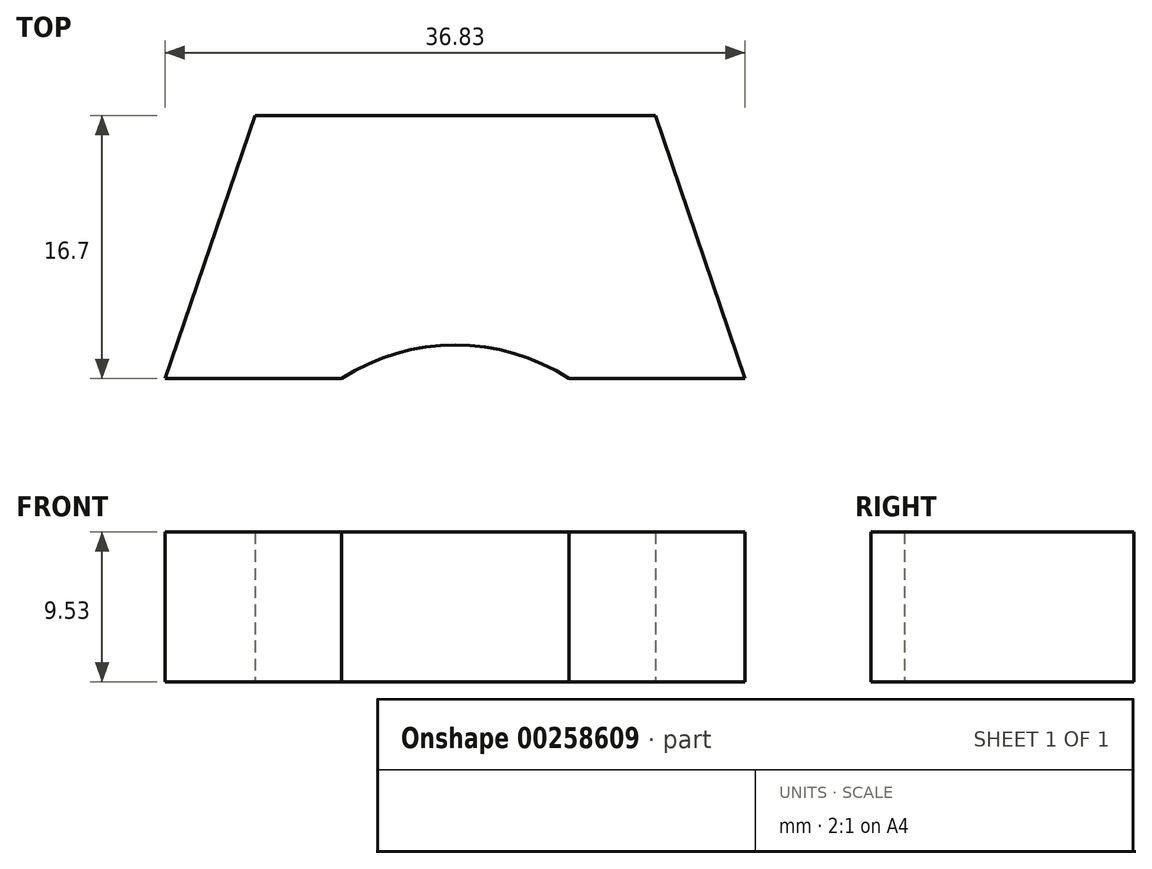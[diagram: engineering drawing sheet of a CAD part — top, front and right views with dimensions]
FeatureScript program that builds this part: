
annotation { "Feature Type Name" : "Feature", "Feature Type Description" : "" }
export const myFeature = defineFeature(function(context is Context, id is Id, definition is map)
    precondition{}
    {
        {
            var Q0;
            Q0=qCreatedBy(makeId("Top.planeOp"),FACE);
            var sketch = newSketch(context, id + "F0", { "sketchPlane" : qUnion([Q0])});
            skLineSegment(sketch, "E0", {"start": v(45.7, 81.96) * mm, "end": v(79.7, 81.96) * mm});
            skLineSegment(sketch, "E1", {"start": v(45.7, 81.96) * mm, "end": v(35.86, 53.26) * mm});
            skLineSegment(sketch, "E2", {"start": v(35.86, 53.26) * mm, "end": v(89.47, 53.26) * mm});
            skLineSegment(sketch, "E3", {"start": v(89.47, 53.26) * mm, "end": v(79.7, 81.96) * mm});
            skLineSegment(sketch, "E4.0", {"start": v(49.98, 75.96) * mm, "end": v(75.4, 75.96) * mm});
            skLineSegment(sketch, "E4.1", {"start": v(49.98, 75.96) * mm, "end": v(44.26, 59.26) * mm});
            skLineSegment(sketch, "E4.2", {"start": v(44.26, 59.26) * mm, "end": v(55.47, 59.26) * mm});
            skLineSegment(sketch, "E4.3", {"start": v(81.09, 59.26) * mm, "end": v(75.4, 75.96) * mm});
            skLineSegment(sketch, "E5", {"start": v(35.86, 53.26) * mm, "end": v(35.86, 42.84) * mm});
            skLineSegment(sketch, "E6", {"start": v(35.86, 42.84) * mm, "end": v(89.47, 42.84) * mm});
            skLineSegment(sketch, "E7", {"start": v(89.47, 42.84) * mm, "end": v(89.47, 53.26) * mm});
            skLineSegment(sketch, "E8", {"start": v(35.86, 48.05) * mm, "end": v(89.47, 48.05) * mm, "construction": true});
            skLineSegment(sketch, "E9", {"start": v(62.7, 81.96) * mm, "end": v(62.7, 14.67) * mm, "construction": true});
            skArc(sketch, "E10", {"start": v(69.91, 59.26) * mm, "mid": v(62.7, 61.38) * mm, "end": v(55.47, 59.26) * mm});
            skPoint(sketch, "E10.centerSnap0", {"position": v(62.7, 48.31) * mm});
            skLineSegment(sketch, "E11.trimOffspring", {"start": v(69.91, 59.26) * mm, "end": v(81.09, 59.26) * mm});
            skArc(sketch, "E12.trimOffspring", {"start": v(50.42, 53.26) * mm, "mid": v(62.7, 34.71) * mm, "end": v(74.97, 53.26) * mm});
            skLineSegment(sketch, "E13", {"start": v(49.98, 75.96) * mm, "end": v(45.7, 81.96) * mm, "construction": true});
            skSolve(sketch);
        }
        {
            var Q0;
            Q0=makeQuery(id+"F0.imprint","IMPRINT",FACE,{"disambiguationData":[TD([[makeQuery(id+"F0.imprint","IMPRINT",EDGE,{"derivedFrom":sQuery(id+"F0.wireOp",EDGE,"E4.0")}),-1.0]])]});
            extrude(context, id + "F1", {"entities" : qUnion([Q0]), "depth" : 9.52 * mm});
        }
    });
